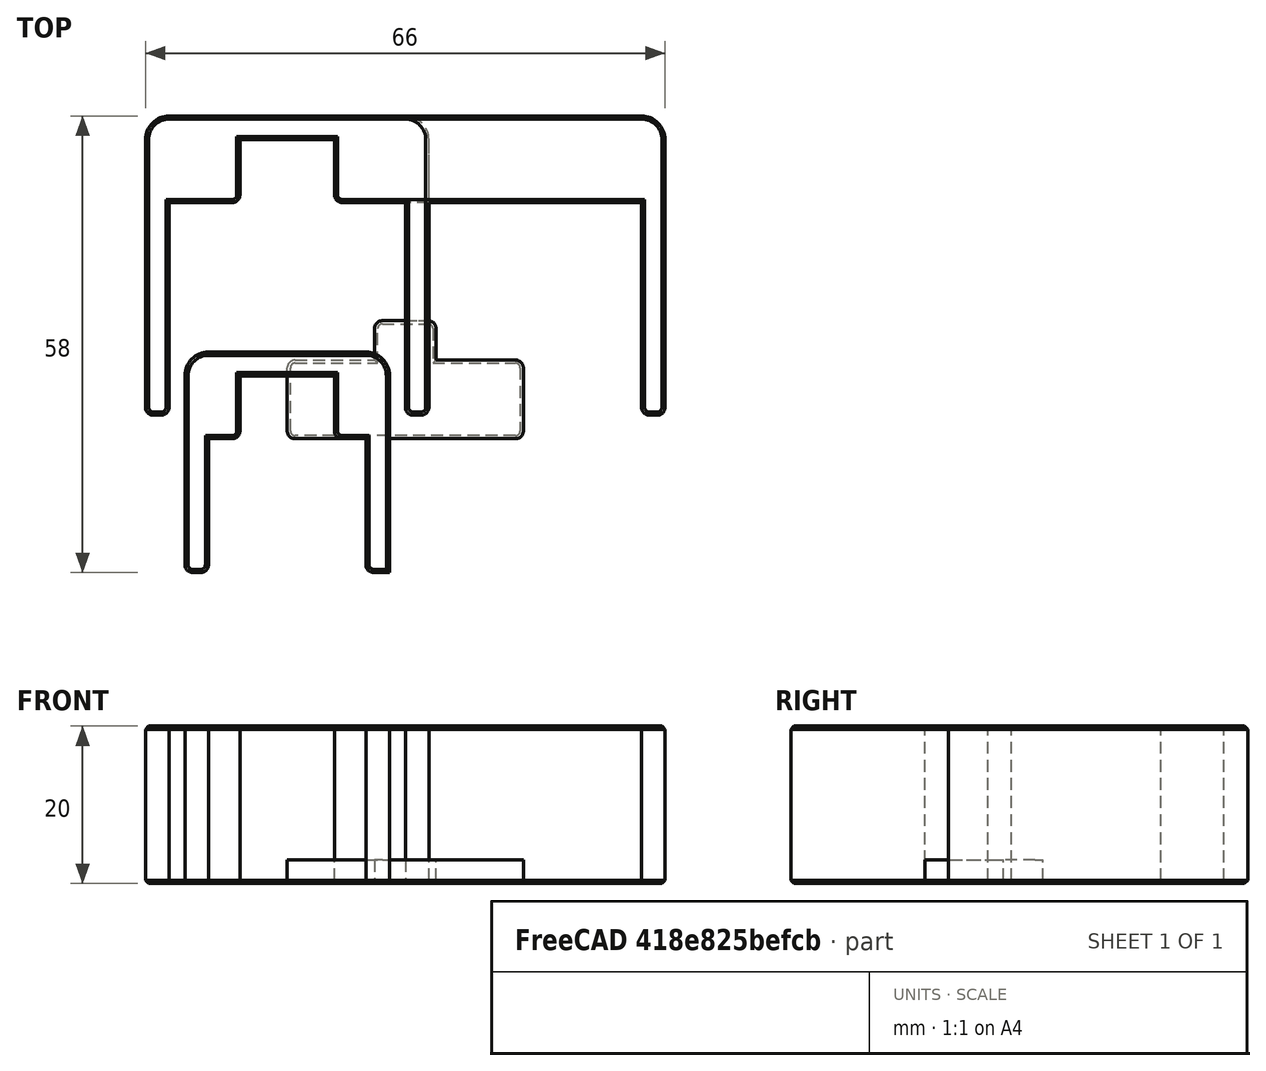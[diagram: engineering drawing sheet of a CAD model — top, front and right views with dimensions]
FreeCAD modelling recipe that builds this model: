
FCSTD DOCUMENT  (FreeCAD 0.19R24291 (Git))
Label: rail-aligner
License: Other
LicenseURL: GPL3
objects: Part::Box×12, Part::Fillet×10, Part::Chamfer×5, Part::MultiFuse×4, Part::Cut×4
note: 35 computed .brp shape members not serialized (recipe doc carries the construction recipe); baked Part::Feature solids carry a one-line shape summary decoded from their .brp

FEATURE [Part::Box] Box  label="Cube"
  AttacherType = Attacher::AttachEngine3D
  Height = 4
  Length = 30
  Width = 10
FEATURE [Part::Box] Box001  label="Cube001"
  AttacherType = Attacher::AttachEngine3D
  Height = 4
  Length = 7.8
  Placement = pos=(11.1,5,0) rot=(0,0,1;0rad)
  Width = 10
FEATURE [Part::Fillet] Fillet
  Base = -> Box
  Edges = 4 edges r=1: [Edge1,Edge3,Edge5,Edge7]
FEATURE [Part::Fillet] Fillet001
  Base = -> Box001
  Edges = 2 edges r=1: [Edge3,Edge7]
FEATURE [Part::Chamfer] Chamfer
  Base = -> Fillet
  Edges = 8 edges r=0.4: [Edge3,Edge12,Edge14,Edge16,Edge17,Edge18,Edge19,Edge20]
FEATURE [Part::Chamfer] Chamfer001
  Base = -> Fillet001
  Edges = 6 edges r=0.4: [Edge3,Edge10,Edge12,Edge14,Edge15,Edge16]
FEATURE [Part::MultiFuse] Fusion
  Shapes = -> [Chamfer,Chamfer001]
FEATURE [Part::Box] Box002  label="Cube002"
  AttacherType = Attacher::AttachEngine3D
  Height = 10
  Length = 30
  Placement = pos=(0,0,3) rot=(0,0,1;0rad)
  Width = 15
FEATURE [Part::Cut] Cut
  Base = -> Fusion
  Tool = -> Box002
FEATURE [Part::Box] Box003  label="Cube003"
  AttacherType = Attacher::AttachEngine3D
  Height = 20
  Length = 36
  Placement = pos=(-18,3,0) rot=(0,0,1;0rad)
  Width = 38
FEATURE [Part::Box] Box004  label="Cube004"
  AttacherType = Attacher::AttachEngine3D
  Height = 20
  Length = 30
  Placement = pos=(-15,0,0) rot=(0,0,1;0rad)
  Width = 30
FEATURE [Part::Box] Box005  label="Cube005"
  AttacherType = Attacher::AttachEngine3D
  Height = 20
  Length = 12
  Placement = pos=(-6,30,0) rot=(0,0,1;0rad)
  Width = 8
FEATURE [Part::Fillet] Fillet002
  Base = -> Box003
  Edges = 2 edges r=3: [Edge3,Edge7]
FEATURE [Part::Fillet] Fillet003  label="30-base"
  Base = -> Fillet002
  Edges = 2 edges r=1: [Edge2,Edge13]
FEATURE [Part::Box] Box006  label="Cube006"
  AttacherType = Attacher::AttachEngine3D
  Height = 20
  Length = 66
  Placement = pos=(-18,3,0) rot=(0,0,1;0rad)
  Width = 38
FEATURE [Part::Fillet] Fillet004
  Base = -> Box006
  Edges = 2 edges r=3: [Edge3,Edge7]
FEATURE [Part::Fillet] Fillet005  label="60-base"
  Base = -> Fillet004
  Edges = 2 edges r=1: [Edge2,Edge13]
FEATURE [Part::MultiFuse] Fusion001
  Shapes = -> [Box004,Box005]
FEATURE [Part::Box] Box007  label="Cube007"
  AttacherType = Attacher::AttachEngine3D
  Height = 20
  Length = 60
  Placement = pos=(-15,0,0) rot=(0,0,1;0rad)
  Width = 30
FEATURE [Part::Box] Box008  label="Cube008"
  AttacherType = Attacher::AttachEngine3D
  Height = 20
  Length = 12
  Placement = pos=(-6,30,0) rot=(0,0,1;0rad)
  Width = 8
FEATURE [Part::Cut] Cut001
  Base = -> Fillet003
  Tool = -> Fusion001
FEATURE [Part::Fillet] Fillet006
  Base = -> Cut001
  Edges = 4 edges r=1: [Edge41,Edge43,Edge46,Edge48]
FEATURE [Part::Chamfer] Chamfer002  label="30-spacer"
  Base = -> Fillet006
  Edges = 40 edges r=0.4: [Edge1,Edge2,Edge3,Edge4,Edge5,Edge6,Edge7,Edge8,Edge9,Edge10,Edge11,Edge12,Edge13,Edge14,Edge15,Edge16,Edge17,Edge18,Edge19,Edge20,Edge21,Edge25,Edge26,Edge28,Edge30,Edge32,Edge34,Edge36,Edge38,Edge40,Edge42,Edge44,Edge47,Edge49,Edge50,Edge52,Edge54,Edge56,Edge58,Edge60]
FEATURE [Part::MultiFuse] Fusion002
  Shapes = -> [Box007,Box008]
FEATURE [Part::Cut] Cut002
  Base = -> Fillet005
  Tool = -> Fusion002
FEATURE [Part::Fillet] Fillet007
  Base = -> Cut002
  Edges = 4 edges r=1: [Edge41,Edge43,Edge46,Edge48]
FEATURE [Part::Chamfer] Chamfer003  label="60-spacer"
  Base = -> Fillet007
  Edges = 40 edges r=0.4: [Edge1,Edge2,Edge3,Edge4,Edge5,Edge6,Edge7,Edge8,Edge9,Edge10,Edge11,Edge12,Edge13,Edge14,Edge15,Edge16,Edge17,Edge18,Edge19,Edge20,Edge21,Edge25,Edge26,Edge28,Edge30,Edge32,Edge34,Edge36,Edge38,Edge40,Edge42,Edge44,Edge47,Edge49,Edge50,Edge52,Edge54,Edge56,Edge58,Edge60]
FEATURE [Part::Box] Box009  label="Cube009"
  AttacherType = Attacher::AttachEngine3D
  Height = 20
  Length = 12
  Placement = pos=(-6,0,0) rot=(0,0,1;0rad)
  Width = 8
FEATURE [Part::Box] Box010  label="Cube010"
  AttacherType = Attacher::AttachEngine3D
  Height = 20
  Length = 20
  Placement = pos=(-10,-20,0) rot=(0,0,1;0rad)
  Width = 20
FEATURE [Part::Box] Box011  label="Cube011"
  AttacherType = Attacher::AttachEngine3D
  Height = 20
  Length = 26
  Placement = pos=(-13,-17,0) rot=(0,0,1;0rad)
  Width = 28
FEATURE [Part::MultiFuse] Fusion003
  Shapes = -> [Box010,Box009]
FEATURE [Part::Cut] Cut003
  Base = -> Box011
  Tool = -> Fusion003
FEATURE [Part::Fillet] Fillet008
  Base = -> Cut003
  Edges = 2 edges r=3: [Edge3,Edge19]
FEATURE [Part::Fillet] Fillet009
  Base = -> Fillet008
  Edges = 5 edges r=1: [Edge2,Edge21,Edge36,Edge39,Edge40]
FEATURE [Part::Chamfer] Chamfer004
  Base = -> Fillet009
  Edges = 38 edges r=0.4: [Edge1,Edge3,Edge5,Edge6,Edge7,Edge8,Edge9,Edge10,Edge11,Edge12,Edge13,Edge14,Edge15,Edge16,Edge17,Edge18,Edge19,Edge20,Edge21,Edge22,Edge23,Edge25,Edge27,Edge28,Edge29,Edge30,Edge31,Edge32,Edge33,Edge34,Edge35,Edge36,Edge37,Edge38,Edge39,Edge40,Edge41,Edge42]
